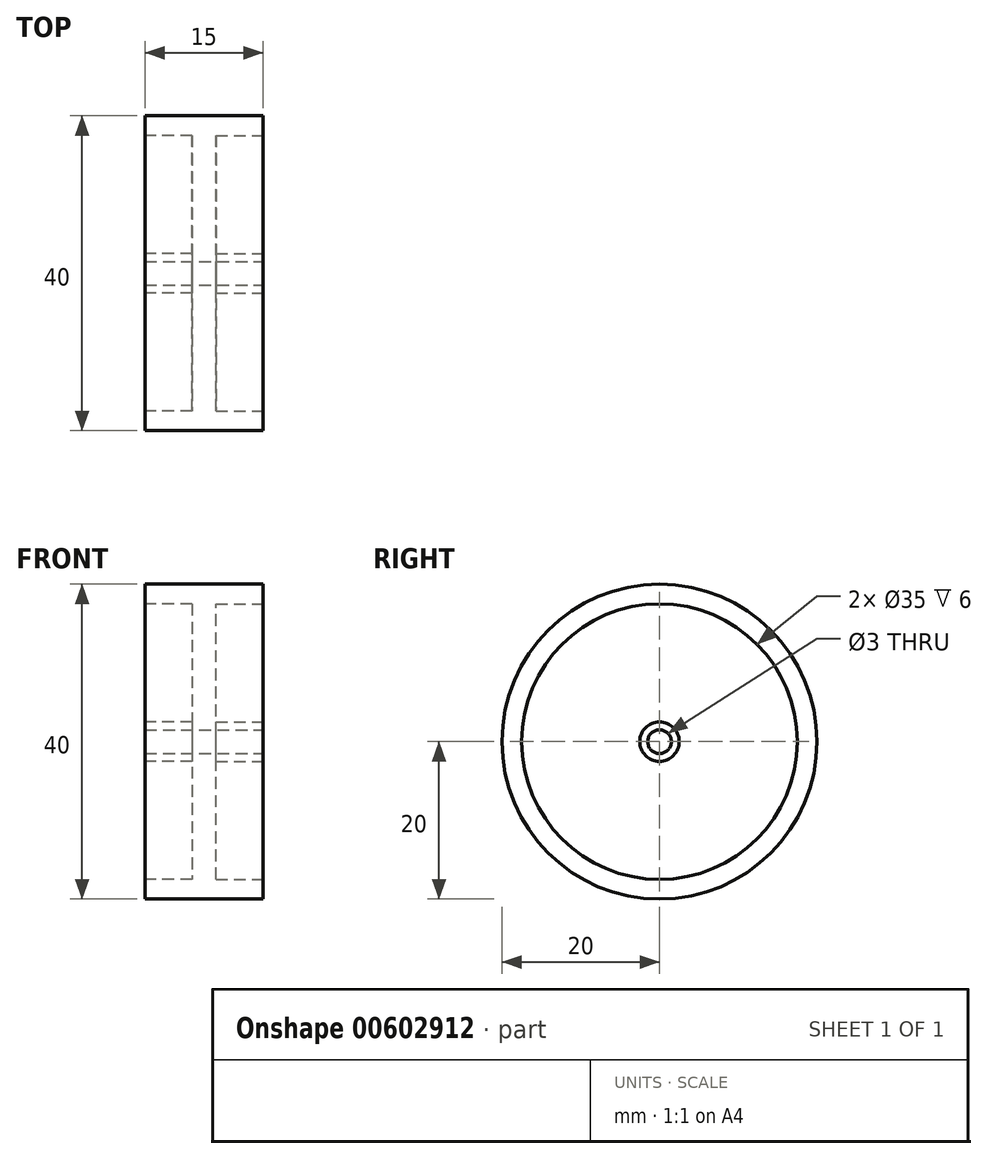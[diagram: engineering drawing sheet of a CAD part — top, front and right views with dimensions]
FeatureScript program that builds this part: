
annotation { "Feature Type Name" : "Feature", "Feature Type Description" : "" }
export const myFeature = defineFeature(function(context is Context, id is Id, definition is map)
    precondition{}
    {
        {
            var Q0;
            Q0=qCreatedBy(makeId("Right.planeOp"),FACE);
            var sketch = newSketch(context, id + "F0", { "sketchPlane" : qUnion([Q0])});
            skCircle(sketch, "E0", {"center": v(0, 0) * mm, "radius": 20 * mm});
            skSolve(sketch);
        }
        {
            var Q0;
            Q0=makeQuery(id+"F0.imprint","IMPRINT",FACE,{"disambiguationData":[TD([[makeQuery(id+"F0.imprint","IMPRINT",EDGE,{"derivedFrom":sQuery(id+"F0.wireOp",EDGE,"E0")}),1.0]])]});
            extrude(context, id + "F1", {"entities" : qUnion([Q0]), "depth" : 15 * mm, "offsetDistance" : 25 * mm});
        }
        {
            var Q0;
            Q0=makeQuery(id+"F1.opExtrude","CAP_FACE",FACE,{"disambiguationData":[OSD([sQuery(id+"F0.wireOp",EDGE,"E0")])],"isStart":false});
            var sketch = newSketch(context, id + "F2", { "sketchPlane" : qUnion([Q0])});
            skCircle(sketch, "E1", {"center": v(0, 0) * mm, "radius": 17.5 * mm});
            skCircle(sketch, "E2", {"center": v(0, 0) * mm, "radius": 2.5 * mm});
            skCircle(sketch, "E3", {"center": v(0, 0) * mm, "radius": 1.5 * mm});
            skSolve(sketch);
        }
        {
            var Q0;
            Q0=makeQuery(id+"F2.imprint","IMPRINT",FACE,{"disambiguationData":[TD([[makeQuery(id+"F2.imprint","IMPRINT",EDGE,{"derivedFrom":sQuery(id+"F2.wireOp",EDGE,"E1")}),1.0]])]});
            extrude(context, id + "F3", {"entities" : qUnion([Q0]), "operationType" : NewBodyOperationType.REMOVE, "oppositeDirection" : true, "depth" : 6 * mm, "offsetDistance" : 25 * mm});
        }
        {
            var Q0;
            Q0=makeQuery(id+"F3.boolean.opBoolean","SPLIT",FACE,{"disambiguationData":[TD([makeQuery(id+"F3.opExtrude","SWEPT_FACE",FACE,{"disambiguationData":[OSD([sQuery(id+"F2.wireOp",EDGE,"E2")])]})])],"derivedFrom":makeQuery(id+"F1.opExtrude","CAP_FACE",FACE,{"disambiguationData":[OSD([sQuery(id+"F0.wireOp",EDGE,"E0")])],"isStart":false})});
            var sketch = newSketch(context, id + "F4", { "sketchPlane" : qUnion([Q0])});
            skCircle(sketch, "E4", {"center": v(0, 0) * mm, "radius": 1.5 * mm});
            skSolve(sketch);
        }
        {
            var Q0;
            Q0=makeQuery(id+"F4.imprint","IMPRINT",FACE,{"disambiguationData":[TD([[makeQuery(id+"F4.imprint","IMPRINT",EDGE,{"derivedFrom":sQuery(id+"F4.wireOp",EDGE,"E4")}),1.0]])]});
            extrude(context, id + "F5", {"entities" : qUnion([Q0]), "operationType" : NewBodyOperationType.REMOVE, "oppositeDirection" : true, "depth" : 25 * mm, "offsetDistance" : 25 * mm});
        }
        {
            var Q0;
            Q0=makeQuery(id+"F1.opExtrude","CAP_FACE",FACE,{"disambiguationData":[OSD([sQuery(id+"F0.wireOp",EDGE,"E0")])],"isStart":true});
            var sketch = newSketch(context, id + "F6", { "sketchPlane" : qUnion([Q0])});
            skCircle(sketch, "E5", {"center": v(0, 0) * mm, "radius": 2.5 * mm});
            skCircle(sketch, "E6", {"center": v(0, 0) * mm, "radius": 17.5 * mm});
            skSolve(sketch);
        }
        {
            var Q0;
            Q0=makeQuery(id+"F6.imprint","IMPRINT",FACE,{"disambiguationData":[TD([[makeQuery(id+"F6.imprint","IMPRINT",EDGE,{"derivedFrom":sQuery(id+"F6.wireOp",EDGE,"E5")}),-1.0]])]});
            extrude(context, id + "F7", {"entities" : qUnion([Q0]), "operationType" : NewBodyOperationType.REMOVE, "oppositeDirection" : true, "depth" : 6 * mm, "offsetDistance" : 25 * mm});
        }
    });
